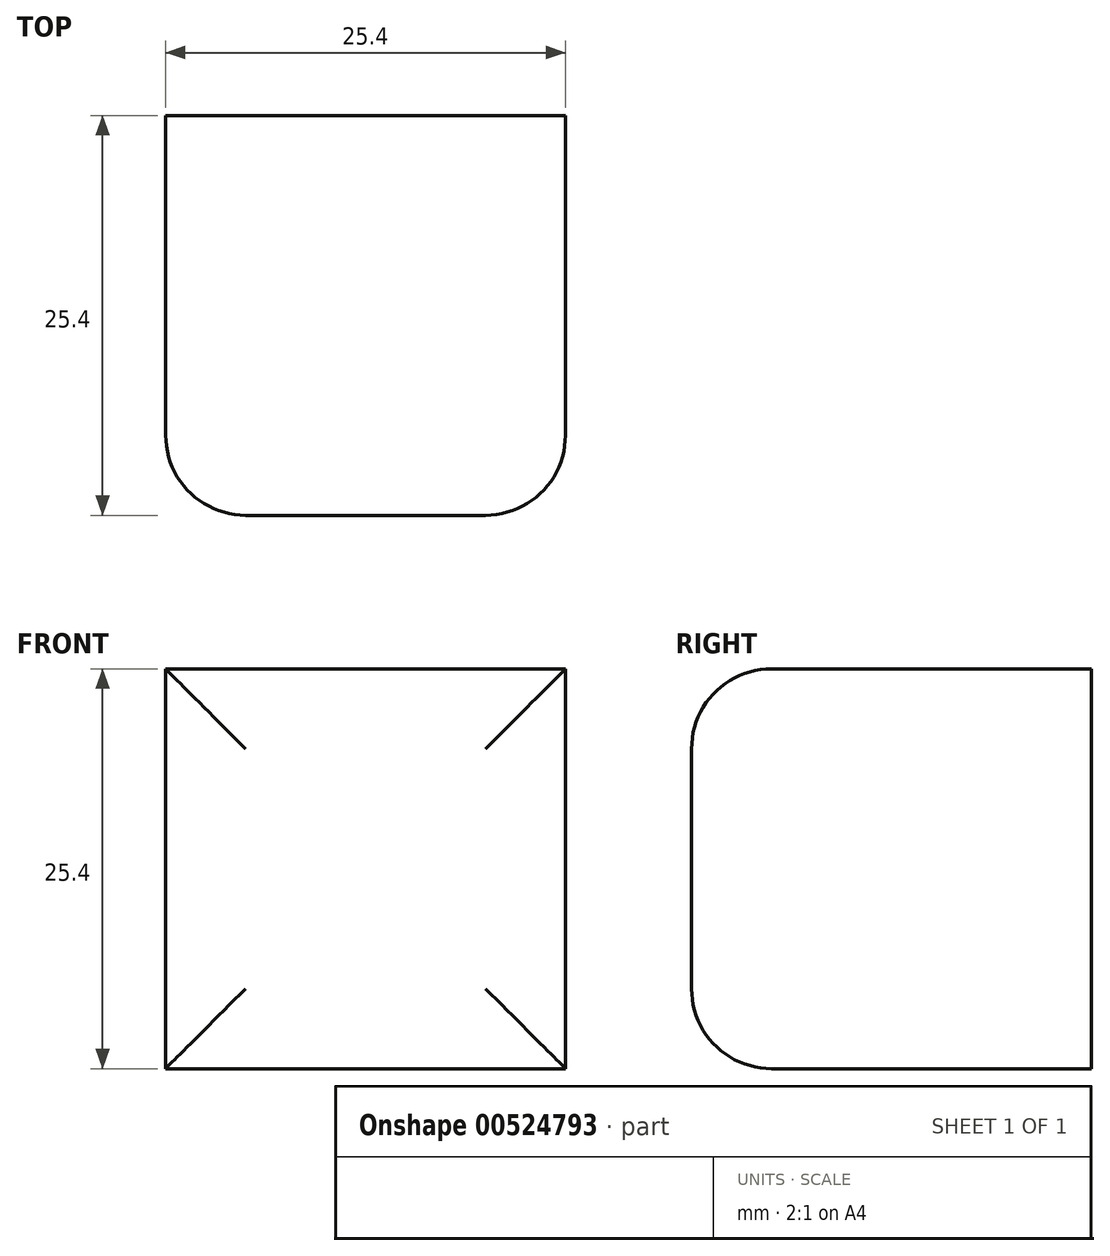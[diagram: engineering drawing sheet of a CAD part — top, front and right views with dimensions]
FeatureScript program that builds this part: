
annotation { "Feature Type Name" : "Feature", "Feature Type Description" : "" }
export const myFeature = defineFeature(function(context is Context, id is Id, definition is map)
    precondition{}
    {
        {
            var Q0;
            Q0=qCreatedBy(makeId("Front.planeOp"),FACE);
            var sketch = newSketch(context, id + "F0", { "sketchPlane" : qUnion([Q0])});
            skLineSegment(sketch, "E0.bottom", {"start": v(0, 0) * mm, "end": v(25.4, 0) * mm});
            skLineSegment(sketch, "E0.top", {"start": v(0, 25.4) * mm, "end": v(25.4, 25.4) * mm});
            skLineSegment(sketch, "E0.left", {"start": v(0, 0) * mm, "end": v(0, 25.4) * mm});
            skLineSegment(sketch, "E0.right", {"start": v(25.4, 0) * mm, "end": v(25.4, 25.4) * mm});
            skSolve(sketch);
        }
        {
            var Q0;
            Q0=makeQuery(id+"F0.imprint","IMPRINT",FACE,{"disambiguationData":[TD([[makeQuery(id+"F0.imprint","IMPRINT",EDGE,{"derivedFrom":sQuery(id+"F0.wireOp",EDGE,"E0.bottom")}),1.0]])]});
            extrude(context, id + "F1", {"entities" : qUnion([Q0]), "depth" : 25.4 * mm, "offsetDistance" : 25.4 * mm});
        }
        {
            var Q0;
            Q0=makeQuery(id+"F1.opExtrude","CAP_FACE",FACE,{"disambiguationData":[OSD([sQuery(id+"F0.wireOp",EDGE,"E0.bottom"),sQuery(id+"F0.wireOp",EDGE,"E0.top"),sQuery(id+"F0.wireOp",EDGE,"E0.left"),sQuery(id+"F0.wireOp",EDGE,"E0.right")])],"isStart":false});
            fillet(context, id + "F2", {"entities" : qUnion([Q0]), "radius" : 5.08 * mm, "tangentPropagation" : true, "allowEdgeOverflow" : false});
        }
    });
